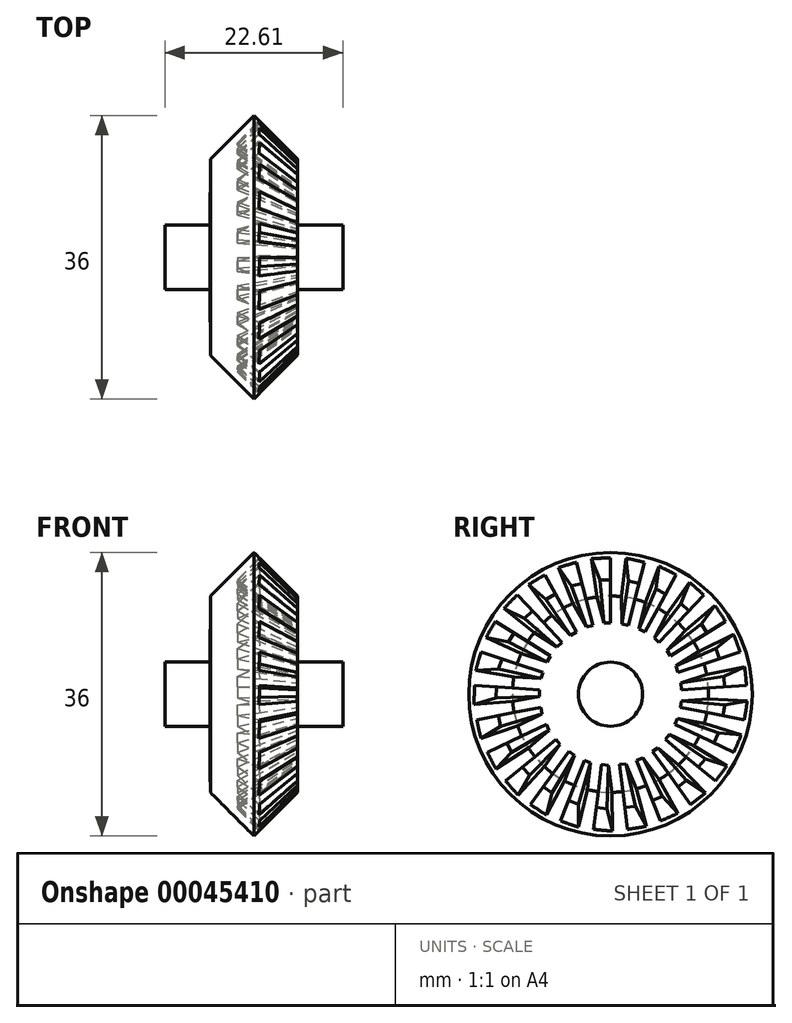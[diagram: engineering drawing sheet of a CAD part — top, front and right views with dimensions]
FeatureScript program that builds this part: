
annotation { "Feature Type Name" : "Feature", "Feature Type Description" : "" }
export const myFeature = defineFeature(function(context is Context, id is Id, definition is map)
    precondition{}
    {
        {
            var Q0;
            Q0=qCreatedBy(makeId("Front.planeOp"),FACE);
            var sketch = newSketch(context, id + "F0", { "sketchPlane" : qUnion([Q0])});
            skLineSegment(sketch, "E0", {"start": v(0.01, 12.47) * mm, "end": v(5.55, 18) * mm});
            skLineSegment(sketch, "E1", {"start": v(5.55, 18) * mm, "end": v(11.08, 12.47) * mm});
            skLineSegment(sketch, "E2", {"start": v(11.08, 12.47) * mm, "end": v(11.08, 4.08) * mm});
            skLineSegment(sketch, "E3", {"start": v(11.08, 4.08) * mm, "end": v(16.85, 4.08) * mm});
            skLineSegment(sketch, "E4", {"start": v(16.85, 4.08) * mm, "end": v(16.85, 0) * mm});
            skLineSegment(sketch, "E5", {"start": v(16.85, 0) * mm, "end": v(0, 0) * mm});
            skLineSegment(sketch, "E6", {"start": v(0, 4.08) * mm, "end": v(-5.76, 4.08) * mm});
            skLineSegment(sketch, "E7", {"start": v(-5.76, 4.08) * mm, "end": v(-5.76, 0) * mm});
            skLineSegment(sketch, "E8", {"start": v(-5.76, 0) * mm, "end": v(0, 0) * mm});
            skLineSegment(sketch, "E9", {"start": v(0, 4.08) * mm, "end": v(0.01, 12.47) * mm});
            skSolve(sketch);
        }
        {
            var Q0;
            Q0=makeQuery(id+"F0.imprint","IMPRINT",FACE,{"disambiguationData":[TD([[makeQuery(id+"F0.imprint","IMPRINT",EDGE,{"derivedFrom":sQuery(id+"F0.wireOp",EDGE,"E0")}),-1.0]])]});
            var Q1;
            Q1=sQuery(id+"F0.wireOp",EDGE,"E5");
            revolve(context, id + "F1", {"entities" : qUnion([Q0]), "axis" : qUnion([Q1]), "revolveType" : RevolveType.FULL});
        }
        {
            var Q0;
            Q0=qCreatedBy(makeId("Front.planeOp"),FACE);
            var sketch = newSketch(context, id + "F2", { "sketchPlane" : qUnion([Q0])});
            skLineSegment(sketch, "E10", {"start": v(0, 0) * mm, "end": v(21.89, 0) * mm, "construction": true});
            skLineSegment(sketch, "E11", {"start": v(5.55, 18) * mm, "end": v(11.08, 12.47) * mm, "construction": true});
            skLineSegment(sketch, "E12", {"start": v(11.08, 12.47) * mm, "end": v(23.55, 0) * mm, "construction": true});
            skLineSegment(sketch, "E13", {"start": v(23.55, 0) * mm, "end": v(21.89, 0) * mm, "construction": true});
            skLineSegment(sketch, "E14", {"start": v(5.55, 18) * mm, "end": v(0, 12.45) * mm, "construction": true});
            skSolve(sketch);
        }
        {
            var Q0;
            Q0=sQuery(id+"F2.wireOp",EDGE,"E14");
            cPlane(context, id + "F3", {"entities" : qUnion([Q0]), "cplaneType" : CPlaneType.LINE_ANGLE, "offset" : 150 * mm, "angle" : 90 * degree, "width" : 150 * mm, "height" : 150 * mm});
        }
        {
            var Q0;
            Q0=qCreatedBy(id+"F3.planeOp",FACE);
            cPlane(context, id + "F4", {"entities" : qUnion([Q0]), "cplaneType" : CPlaneType.OFFSET, "offset" : 1 * mm, "oppositeDirection" : true, "width" : 150 * mm, "height" : 150 * mm});
        }
        {
            var Q0;
            Q0=qCreatedBy(id+"F4.planeOp",FACE);
            var sketch = newSketch(context, id + "F5", { "sketchPlane" : qUnion([Q0])});
            skLineSegment(sketch, "E15.0", {"start": v(0, 16.65) * mm, "end": v(0, 8.8) * mm, "construction": true});
            skLineSegment(sketch, "E16", {"start": v(0, 12.73) * mm, "end": v(1.37, 12.73) * mm});
            skLineSegment(sketch, "E17", {"start": v(1.37, 12.73) * mm, "end": v(2.44, 16.65) * mm});
            skLineSegment(sketch, "E18", {"start": v(2.44, 16.65) * mm, "end": v(0, 16.65) * mm});
            skLineSegment(sketch, "E19", {"start": v(0, 12.73) * mm, "end": v(0, 16.65) * mm});
            skSolve(sketch);
        }
        {
            var Q1;
            Q1=makeQuery(id+"F5.imprint","IMPRINT",FACE,{"disambiguationData":[TD([[makeQuery(id+"F5.imprint","IMPRINT",EDGE,{"derivedFrom":sQuery(id+"F5.wireOp",EDGE,"E16")}),1.0]])]});
            var Q2;
            Q2=sQuery(id+"F2.wireOp",VERTEX,"E13.start");
            loft(context, id + "F6", {"sheetProfilesArray" : [{ "sheetProfileEntities" : qUnion([Q1]) }, { "sheetProfileEntities" : qUnion([Q2]) }]});
        }
        {
            var Q0;
            Q0=makeQuery(id+"F6.opLoft","SWEPT_BODY",BODY,{"disambiguationData":[OSD([sQuery(id+"F2.wireOp",VERTEX,"E13.start"),makeQuery(id+"F5.imprint","IMPRINT",FACE,{"disambiguationData":[TD([[makeQuery(id+"F5.imprint","IMPRINT",EDGE,{"derivedFrom":sQuery(id+"F5.wireOp",EDGE,"E16")}),1.0]])]})])]});
            var Q1;
            Q1=makeQuery(id+"F1.opRevolve","SWEPT_EDGE",EDGE,{"disambiguationData":[OSD([sQuery(id+"F0.wireOp",EDGE,"E3"),sQuery(id+"F0.wireOp",EDGE,"E4")])]});
            circularPattern(context, id + "F7", {"entities" : qUnion([Q0]), "axis" : qUnion([Q1]), "angle" : 14.4 * degree, "instanceCount" : 25});
        }
        {
            var Q0;
            Q0=makeQuery(id+"F6.opLoft","SWEPT_BODY",BODY,{"disambiguationData":[OSD([sQuery(id+"F2.wireOp",VERTEX,"E13.start"),makeQuery(id+"F5.imprint","IMPRINT",FACE,{"disambiguationData":[TD([[makeQuery(id+"F5.imprint","IMPRINT",EDGE,{"derivedFrom":sQuery(id+"F5.wireOp",EDGE,"E16")}),1.0]])]})])]});
            var Q1;
            Q1=makeQuery(id+"F7.opPattern","COPY",BODY,{"derivedFrom":makeQuery(id+"F6.opLoft","SWEPT_BODY",BODY,{"disambiguationData":[OSD([sQuery(id+"F2.wireOp",VERTEX,"E13.start"),makeQuery(id+"F5.imprint","IMPRINT",FACE,{"disambiguationData":[TD([[makeQuery(id+"F5.imprint","IMPRINT",EDGE,{"derivedFrom":sQuery(id+"F5.wireOp",EDGE,"E16")}),1.0]])]})])]}),"instanceName":"1"});
            var Q2;
            Q2=makeQuery(id+"F7.opPattern","COPY",BODY,{"derivedFrom":makeQuery(id+"F6.opLoft","SWEPT_BODY",BODY,{"disambiguationData":[OSD([sQuery(id+"F2.wireOp",VERTEX,"E13.start"),makeQuery(id+"F5.imprint","IMPRINT",FACE,{"disambiguationData":[TD([[makeQuery(id+"F5.imprint","IMPRINT",EDGE,{"derivedFrom":sQuery(id+"F5.wireOp",EDGE,"E16")}),1.0]])]})])]}),"instanceName":"2"});
            var Q3;
            Q3=makeQuery(id+"F7.opPattern","COPY",BODY,{"derivedFrom":makeQuery(id+"F6.opLoft","SWEPT_BODY",BODY,{"disambiguationData":[OSD([sQuery(id+"F2.wireOp",VERTEX,"E13.start"),makeQuery(id+"F5.imprint","IMPRINT",FACE,{"disambiguationData":[TD([[makeQuery(id+"F5.imprint","IMPRINT",EDGE,{"derivedFrom":sQuery(id+"F5.wireOp",EDGE,"E16")}),1.0]])]})])]}),"instanceName":"3"});
            var Q4;
            Q4=makeQuery(id+"F7.opPattern","COPY",BODY,{"derivedFrom":makeQuery(id+"F6.opLoft","SWEPT_BODY",BODY,{"disambiguationData":[OSD([sQuery(id+"F2.wireOp",VERTEX,"E13.start"),makeQuery(id+"F5.imprint","IMPRINT",FACE,{"disambiguationData":[TD([[makeQuery(id+"F5.imprint","IMPRINT",EDGE,{"derivedFrom":sQuery(id+"F5.wireOp",EDGE,"E16")}),1.0]])]})])]}),"instanceName":"4"});
            var Q5;
            Q5=makeQuery(id+"F7.opPattern","COPY",BODY,{"derivedFrom":makeQuery(id+"F6.opLoft","SWEPT_BODY",BODY,{"disambiguationData":[OSD([sQuery(id+"F2.wireOp",VERTEX,"E13.start"),makeQuery(id+"F5.imprint","IMPRINT",FACE,{"disambiguationData":[TD([[makeQuery(id+"F5.imprint","IMPRINT",EDGE,{"derivedFrom":sQuery(id+"F5.wireOp",EDGE,"E16")}),1.0]])]})])]}),"instanceName":"5"});
            var Q6;
            Q6=makeQuery(id+"F7.opPattern","COPY",BODY,{"derivedFrom":makeQuery(id+"F6.opLoft","SWEPT_BODY",BODY,{"disambiguationData":[OSD([sQuery(id+"F2.wireOp",VERTEX,"E13.start"),makeQuery(id+"F5.imprint","IMPRINT",FACE,{"disambiguationData":[TD([[makeQuery(id+"F5.imprint","IMPRINT",EDGE,{"derivedFrom":sQuery(id+"F5.wireOp",EDGE,"E16")}),1.0]])]})])]}),"instanceName":"6"});
            var Q7;
            Q7=makeQuery(id+"F7.opPattern","COPY",BODY,{"derivedFrom":makeQuery(id+"F6.opLoft","SWEPT_BODY",BODY,{"disambiguationData":[OSD([sQuery(id+"F2.wireOp",VERTEX,"E13.start"),makeQuery(id+"F5.imprint","IMPRINT",FACE,{"disambiguationData":[TD([[makeQuery(id+"F5.imprint","IMPRINT",EDGE,{"derivedFrom":sQuery(id+"F5.wireOp",EDGE,"E16")}),1.0]])]})])]}),"instanceName":"7"});
            var Q8;
            Q8=makeQuery(id+"F7.opPattern","COPY",BODY,{"derivedFrom":makeQuery(id+"F6.opLoft","SWEPT_BODY",BODY,{"disambiguationData":[OSD([sQuery(id+"F2.wireOp",VERTEX,"E13.start"),makeQuery(id+"F5.imprint","IMPRINT",FACE,{"disambiguationData":[TD([[makeQuery(id+"F5.imprint","IMPRINT",EDGE,{"derivedFrom":sQuery(id+"F5.wireOp",EDGE,"E16")}),1.0]])]})])]}),"instanceName":"8"});
            var Q9;
            Q9=makeQuery(id+"F7.opPattern","COPY",BODY,{"derivedFrom":makeQuery(id+"F6.opLoft","SWEPT_BODY",BODY,{"disambiguationData":[OSD([sQuery(id+"F2.wireOp",VERTEX,"E13.start"),makeQuery(id+"F5.imprint","IMPRINT",FACE,{"disambiguationData":[TD([[makeQuery(id+"F5.imprint","IMPRINT",EDGE,{"derivedFrom":sQuery(id+"F5.wireOp",EDGE,"E16")}),1.0]])]})])]}),"instanceName":"9"});
            var Q10;
            Q10=makeQuery(id+"F7.opPattern","COPY",BODY,{"derivedFrom":makeQuery(id+"F6.opLoft","SWEPT_BODY",BODY,{"disambiguationData":[OSD([sQuery(id+"F2.wireOp",VERTEX,"E13.start"),makeQuery(id+"F5.imprint","IMPRINT",FACE,{"disambiguationData":[TD([[makeQuery(id+"F5.imprint","IMPRINT",EDGE,{"derivedFrom":sQuery(id+"F5.wireOp",EDGE,"E16")}),1.0]])]})])]}),"instanceName":"10"});
            var Q11;
            Q11=makeQuery(id+"F7.opPattern","COPY",BODY,{"derivedFrom":makeQuery(id+"F6.opLoft","SWEPT_BODY",BODY,{"disambiguationData":[OSD([sQuery(id+"F2.wireOp",VERTEX,"E13.start"),makeQuery(id+"F5.imprint","IMPRINT",FACE,{"disambiguationData":[TD([[makeQuery(id+"F5.imprint","IMPRINT",EDGE,{"derivedFrom":sQuery(id+"F5.wireOp",EDGE,"E16")}),1.0]])]})])]}),"instanceName":"11"});
            var Q12;
            Q12=makeQuery(id+"F7.opPattern","COPY",BODY,{"derivedFrom":makeQuery(id+"F6.opLoft","SWEPT_BODY",BODY,{"disambiguationData":[OSD([sQuery(id+"F2.wireOp",VERTEX,"E13.start"),makeQuery(id+"F5.imprint","IMPRINT",FACE,{"disambiguationData":[TD([[makeQuery(id+"F5.imprint","IMPRINT",EDGE,{"derivedFrom":sQuery(id+"F5.wireOp",EDGE,"E16")}),1.0]])]})])]}),"instanceName":"12"});
            var Q13;
            Q13=makeQuery(id+"F7.opPattern","COPY",BODY,{"derivedFrom":makeQuery(id+"F6.opLoft","SWEPT_BODY",BODY,{"disambiguationData":[OSD([sQuery(id+"F2.wireOp",VERTEX,"E13.start"),makeQuery(id+"F5.imprint","IMPRINT",FACE,{"disambiguationData":[TD([[makeQuery(id+"F5.imprint","IMPRINT",EDGE,{"derivedFrom":sQuery(id+"F5.wireOp",EDGE,"E16")}),1.0]])]})])]}),"instanceName":"13"});
            var Q14;
            Q14=makeQuery(id+"F7.opPattern","COPY",BODY,{"derivedFrom":makeQuery(id+"F6.opLoft","SWEPT_BODY",BODY,{"disambiguationData":[OSD([sQuery(id+"F2.wireOp",VERTEX,"E13.start"),makeQuery(id+"F5.imprint","IMPRINT",FACE,{"disambiguationData":[TD([[makeQuery(id+"F5.imprint","IMPRINT",EDGE,{"derivedFrom":sQuery(id+"F5.wireOp",EDGE,"E16")}),1.0]])]})])]}),"instanceName":"14"});
            var Q15;
            Q15=makeQuery(id+"F7.opPattern","COPY",BODY,{"derivedFrom":makeQuery(id+"F6.opLoft","SWEPT_BODY",BODY,{"disambiguationData":[OSD([sQuery(id+"F2.wireOp",VERTEX,"E13.start"),makeQuery(id+"F5.imprint","IMPRINT",FACE,{"disambiguationData":[TD([[makeQuery(id+"F5.imprint","IMPRINT",EDGE,{"derivedFrom":sQuery(id+"F5.wireOp",EDGE,"E16")}),1.0]])]})])]}),"instanceName":"15"});
            var Q16;
            Q16=makeQuery(id+"F7.opPattern","COPY",BODY,{"derivedFrom":makeQuery(id+"F6.opLoft","SWEPT_BODY",BODY,{"disambiguationData":[OSD([sQuery(id+"F2.wireOp",VERTEX,"E13.start"),makeQuery(id+"F5.imprint","IMPRINT",FACE,{"disambiguationData":[TD([[makeQuery(id+"F5.imprint","IMPRINT",EDGE,{"derivedFrom":sQuery(id+"F5.wireOp",EDGE,"E16")}),1.0]])]})])]}),"instanceName":"16"});
            var Q17;
            Q17=makeQuery(id+"F7.opPattern","COPY",BODY,{"derivedFrom":makeQuery(id+"F6.opLoft","SWEPT_BODY",BODY,{"disambiguationData":[OSD([sQuery(id+"F2.wireOp",VERTEX,"E13.start"),makeQuery(id+"F5.imprint","IMPRINT",FACE,{"disambiguationData":[TD([[makeQuery(id+"F5.imprint","IMPRINT",EDGE,{"derivedFrom":sQuery(id+"F5.wireOp",EDGE,"E16")}),1.0]])]})])]}),"instanceName":"17"});
            var Q18;
            Q18=makeQuery(id+"F7.opPattern","COPY",BODY,{"derivedFrom":makeQuery(id+"F6.opLoft","SWEPT_BODY",BODY,{"disambiguationData":[OSD([sQuery(id+"F2.wireOp",VERTEX,"E13.start"),makeQuery(id+"F5.imprint","IMPRINT",FACE,{"disambiguationData":[TD([[makeQuery(id+"F5.imprint","IMPRINT",EDGE,{"derivedFrom":sQuery(id+"F5.wireOp",EDGE,"E16")}),1.0]])]})])]}),"instanceName":"18"});
            var Q19;
            Q19=makeQuery(id+"F7.opPattern","COPY",BODY,{"derivedFrom":makeQuery(id+"F6.opLoft","SWEPT_BODY",BODY,{"disambiguationData":[OSD([sQuery(id+"F2.wireOp",VERTEX,"E13.start"),makeQuery(id+"F5.imprint","IMPRINT",FACE,{"disambiguationData":[TD([[makeQuery(id+"F5.imprint","IMPRINT",EDGE,{"derivedFrom":sQuery(id+"F5.wireOp",EDGE,"E16")}),1.0]])]})])]}),"instanceName":"19"});
            var Q20;
            Q20=makeQuery(id+"F7.opPattern","COPY",BODY,{"derivedFrom":makeQuery(id+"F6.opLoft","SWEPT_BODY",BODY,{"disambiguationData":[OSD([sQuery(id+"F2.wireOp",VERTEX,"E13.start"),makeQuery(id+"F5.imprint","IMPRINT",FACE,{"disambiguationData":[TD([[makeQuery(id+"F5.imprint","IMPRINT",EDGE,{"derivedFrom":sQuery(id+"F5.wireOp",EDGE,"E16")}),1.0]])]})])]}),"instanceName":"20"});
            var Q21;
            Q21=makeQuery(id+"F7.opPattern","COPY",BODY,{"derivedFrom":makeQuery(id+"F6.opLoft","SWEPT_BODY",BODY,{"disambiguationData":[OSD([sQuery(id+"F2.wireOp",VERTEX,"E13.start"),makeQuery(id+"F5.imprint","IMPRINT",FACE,{"disambiguationData":[TD([[makeQuery(id+"F5.imprint","IMPRINT",EDGE,{"derivedFrom":sQuery(id+"F5.wireOp",EDGE,"E16")}),1.0]])]})])]}),"instanceName":"21"});
            var Q22;
            Q22=makeQuery(id+"F7.opPattern","COPY",BODY,{"derivedFrom":makeQuery(id+"F6.opLoft","SWEPT_BODY",BODY,{"disambiguationData":[OSD([sQuery(id+"F2.wireOp",VERTEX,"E13.start"),makeQuery(id+"F5.imprint","IMPRINT",FACE,{"disambiguationData":[TD([[makeQuery(id+"F5.imprint","IMPRINT",EDGE,{"derivedFrom":sQuery(id+"F5.wireOp",EDGE,"E16")}),1.0]])]})])]}),"instanceName":"22"});
            var Q23;
            Q23=makeQuery(id+"F7.opPattern","COPY",BODY,{"derivedFrom":makeQuery(id+"F6.opLoft","SWEPT_BODY",BODY,{"disambiguationData":[OSD([sQuery(id+"F2.wireOp",VERTEX,"E13.start"),makeQuery(id+"F5.imprint","IMPRINT",FACE,{"disambiguationData":[TD([[makeQuery(id+"F5.imprint","IMPRINT",EDGE,{"derivedFrom":sQuery(id+"F5.wireOp",EDGE,"E16")}),1.0]])]})])]}),"instanceName":"23"});
            var Q24;
            Q24=makeQuery(id+"F7.opPattern","COPY",BODY,{"derivedFrom":makeQuery(id+"F6.opLoft","SWEPT_BODY",BODY,{"disambiguationData":[OSD([sQuery(id+"F2.wireOp",VERTEX,"E13.start"),makeQuery(id+"F5.imprint","IMPRINT",FACE,{"disambiguationData":[TD([[makeQuery(id+"F5.imprint","IMPRINT",EDGE,{"derivedFrom":sQuery(id+"F5.wireOp",EDGE,"E16")}),1.0]])]})])]}),"instanceName":"24"});
            var Q25;
            Q25=makeQuery(id+"F1.opRevolve","SWEPT_BODY",BODY,{"disambiguationData":[OSD([sQuery(id+"F0.wireOp",EDGE,"E0"),sQuery(id+"F0.wireOp",EDGE,"E1"),sQuery(id+"F0.wireOp",EDGE,"E2"),sQuery(id+"F0.wireOp",EDGE,"E3"),sQuery(id+"F0.wireOp",EDGE,"E4"),sQuery(id+"F0.wireOp",EDGE,"E5"),sQuery(id+"F0.wireOp",EDGE,"E6"),sQuery(id+"F0.wireOp",EDGE,"E7"),sQuery(id+"F0.wireOp",EDGE,"E8"),sQuery(id+"F0.wireOp",EDGE,"E9")])]});
            booleanBodies(context, id + "F8", {"operationType" : BooleanOperationType.SUBTRACTION, "tools" : qUnion([Q0, Q1, Q2, Q3, Q4, Q5, Q6, Q7, Q8, Q9, Q10, Q11, Q12, Q13, Q14, Q15, Q16, Q17, Q18, Q19, Q20, Q21, Q22, Q23, Q24]), "targets" : qUnion([Q25])});
        }
    });
